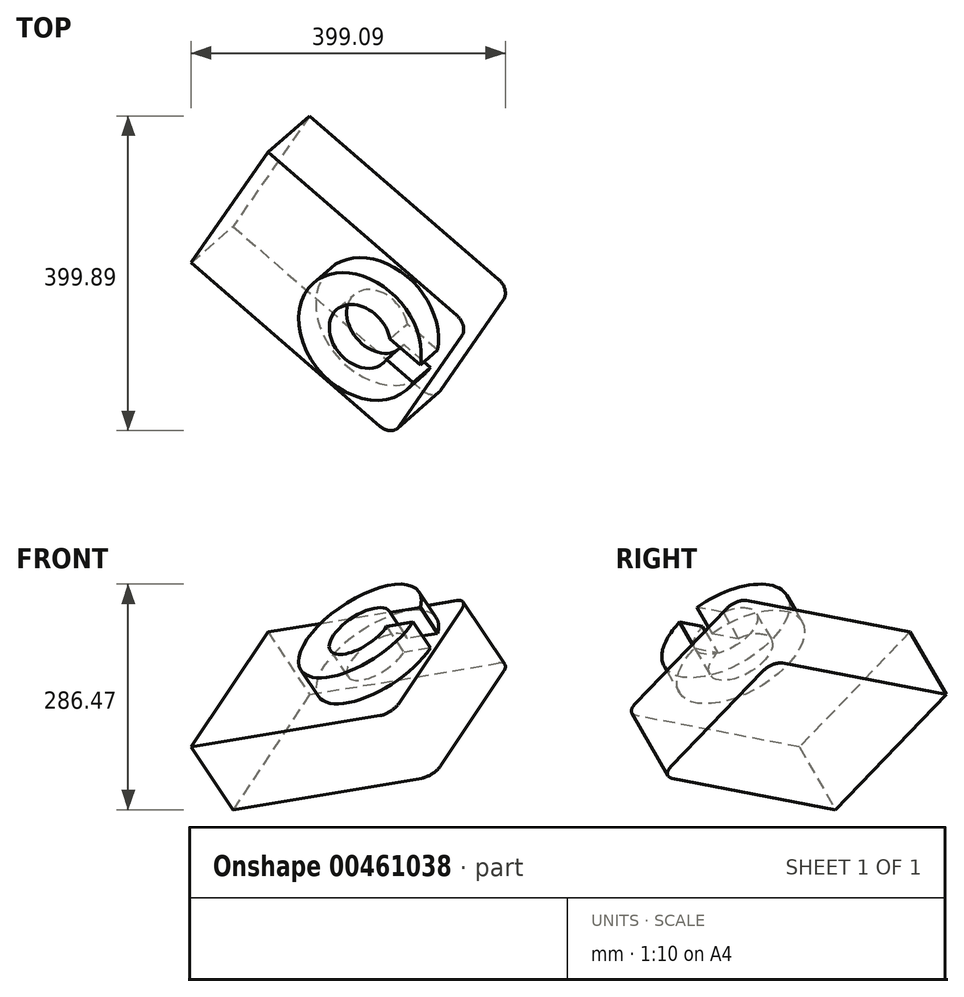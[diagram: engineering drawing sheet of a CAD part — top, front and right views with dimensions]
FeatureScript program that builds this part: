
annotation { "Feature Type Name" : "Feature", "Feature Type Description" : "" }
export const myFeature = defineFeature(function(context is Context, id is Id, definition is map)
    precondition{}
    {
        {
            var Q0;
            Q0=qCreatedBy(makeId("Top.planeOp"),FACE);
            var sketch = newSketch(context, id + "F0", { "sketchPlane" : qUnion([Q0])});
            skArc(sketch, "E0", {"start": v(344.85, 120) * mm, "mid": v(171.3, 74.78) * mm, "end": v(350, 90) * mm});
            skArc(sketch, "E1", {"start": v(293.54, 120) * mm, "mid": v(217.96, 73.94) * mm, "end": v(305, 90) * mm});
            skLineSegment(sketch, "E2.bottom", {"start": v(20, 185) * mm, "end": v(340, 185) * mm});
            skLineSegment(sketch, "E2.top", {"start": v(20, -40) * mm, "end": v(340, -40) * mm});
            skLineSegment(sketch, "E2.left", {"start": v(20, 185) * mm, "end": v(20, -40) * mm});
            skLineSegment(sketch, "E2.right", {"start": v(360, 165) * mm, "end": v(360, -20) * mm});
            skPoint(sketch, "E3.visualSharp", {"position": v(360, 185) * mm});
            skArc(sketch, "E3.filletArc", {"start": v(360, 165) * mm, "mid": v(354.14, 179.14) * mm, "end": v(340, 185) * mm});
            skPoint(sketch, "E4.visualSharp", {"position": v(360, -40) * mm});
            skArc(sketch, "E4.filletArc", {"start": v(340, -40) * mm, "mid": v(354.14, -34.14) * mm, "end": v(360, -20) * mm});
            skLineSegment(sketch, "E5.bottom", {"start": v(305, 90) * mm, "end": v(350, 90) * mm});
            skLineSegment(sketch, "E5.top", {"start": v(293.54, 120) * mm, "end": v(344.85, 120) * mm});
            skSolve(sketch);
        }
        {
            var Q0;
            Q0 = qSketchRegion(id + "F0", true);
            var Q1;
            Q1=makeQuery(id+"F0.imprint","IMPRINT",FACE,{"disambiguationData":[TD([[makeQuery(id+"F0.imprint","IMPRINT",EDGE,{"derivedFrom":sQuery(id+"F0.wireOp",EDGE,"E0")}),1.0]])]});
            extrude(context, id + "F1", {"entities" : qUnion([Q0, Q1]), "depth" : 106 * mm});
        }
        {
            var Q0;
            Q0=makeQuery(id+"F0.imprint","IMPRINT",FACE,{"disambiguationData":[TD([[makeQuery(id+"F0.imprint","IMPRINT",EDGE,{"derivedFrom":sQuery(id+"F0.wireOp",EDGE,"E0")}),1.0]])]});
            extrude(context, id + "F2", {"entities" : qUnion([Q0]), "operationType" : NewBodyOperationType.ADD, "depth" : 150 * mm});
        }
        {
            var Q0;
            Q0=makeQuery(id+"F1.opExtrude","SWEPT_BODY",BODY,{"disambiguationData":[OSD([sQuery(id+"F0.wireOp",EDGE,"E2.bottom"),sQuery(id+"F0.wireOp",EDGE,"E2.top"),sQuery(id+"F0.wireOp",EDGE,"E2.left"),sQuery(id+"F0.wireOp",EDGE,"E2.right"),sQuery(id+"F0.wireOp",EDGE,"E3.filletArc"),sQuery(id+"F0.wireOp",EDGE,"E4.filletArc")])]});
            var Q1;
            Q1=sQuery(id+"F0.wireOp",EDGE,"E2.top");
            var Q2;
            Q2=sQuery(id+"F0.wireOp",EDGE,"E2.top");
            transform(context, id + "F3", {"entities" : qUnion([Q0]), "transformType" : TransformType.ROTATION, "transformAxis" : qUnion([Q2]), "angle" : 30 * degree, "makeCopy" : false});
        }
        {
            var Q0;
            Q0=makeQuery(id+"F1.opExtrude","SWEPT_BODY",BODY,{"disambiguationData":[OSD([sQuery(id+"F0.wireOp",EDGE,"E2.bottom"),sQuery(id+"F0.wireOp",EDGE,"E2.top"),sQuery(id+"F0.wireOp",EDGE,"E2.left"),sQuery(id+"F0.wireOp",EDGE,"E2.right"),sQuery(id+"F0.wireOp",EDGE,"E3.filletArc"),sQuery(id+"F0.wireOp",EDGE,"E4.filletArc")])]});
            var Q1;
            Q1=makeQuery(id+"F1.opExtrude","CAP_EDGE",EDGE,{"disambiguationData":[OSD([sQuery(id+"F0.wireOp",EDGE,"E2.left")])],"isStart":false});
            transform(context, id + "F4", {"entities" : qUnion([Q0]), "transformType" : TransformType.ROTATION, "transformAxis" : qUnion([Q1]), "angle" : 30 * degree, "makeCopy" : false});
        }
        {
            var Q0;
            Q0=makeQuery(id+"F1.opExtrude","SWEPT_BODY",BODY,{"disambiguationData":[OSD([sQuery(id+"F0.wireOp",EDGE,"E2.bottom"),sQuery(id+"F0.wireOp",EDGE,"E2.top"),sQuery(id+"F0.wireOp",EDGE,"E2.left"),sQuery(id+"F0.wireOp",EDGE,"E2.right"),sQuery(id+"F0.wireOp",EDGE,"E3.filletArc"),sQuery(id+"F0.wireOp",EDGE,"E4.filletArc")])]});
            var Q1;
            Q1=makeQuery(id+"F1.opExtrude","SWEPT_EDGE",EDGE,{"disambiguationData":[OSD([sQuery(id+"F0.wireOp",EDGE,"E2.top"),sQuery(id+"F0.wireOp",EDGE,"E2.left")])]});
            transform(context, id + "F5", {"entities" : qUnion([Q0]), "transformType" : TransformType.ROTATION, "transformAxis" : qUnion([Q1]), "angle" : 30 * degree, "makeCopy" : false});
        }
    });
